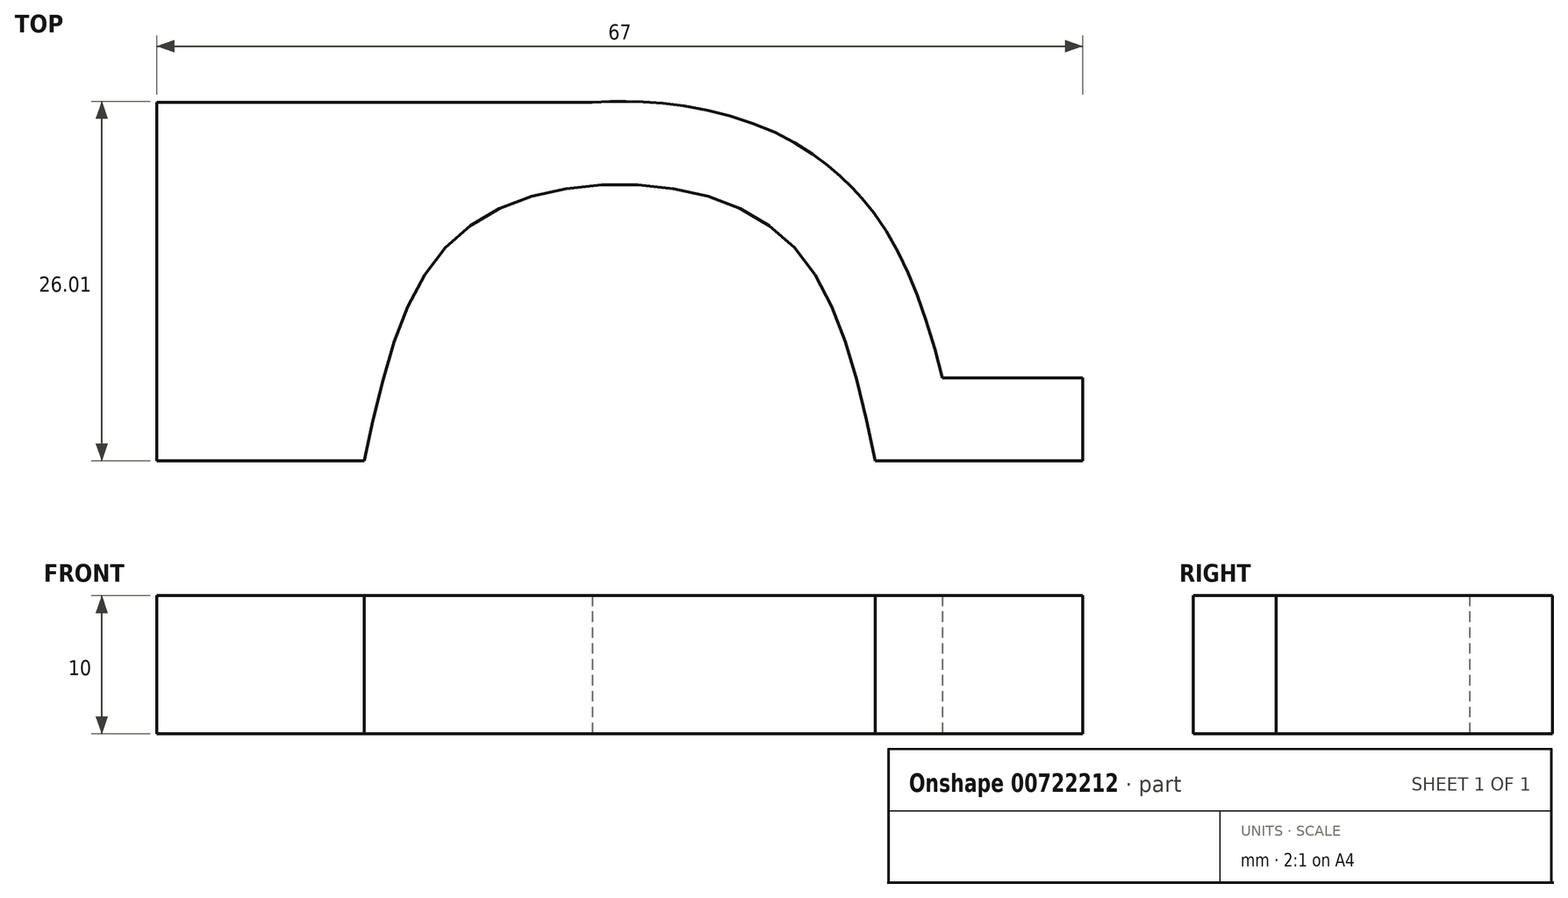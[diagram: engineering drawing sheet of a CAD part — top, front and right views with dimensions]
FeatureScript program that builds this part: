
annotation { "Feature Type Name" : "Feature", "Feature Type Description" : "" }
export const myFeature = defineFeature(function(context is Context, id is Id, definition is map)
    precondition{}
    {
        {
            var Q0;
            Q0=qCreatedBy(makeId("Top.planeOp"),FACE);
            var sketch = newSketch(context, id + "F0", { "sketchPlane" : qUnion([Q0])});
            skFitSpline(sketch, "E0", {"points": [v(-18.5, -20) * mm, v(-12.5, -4.42) * mm, v(0, 0) * mm, v(12.5, -4.42) * mm, v(18.5, -20) * mm], "startDerivative": vector(14.66, 68.17) * mm, "endDerivative": vector(14.66, -68.17) * mm});
            skLineSegment(sketch, "E1", {"start": v(-18.5, -20) * mm, "end": v(-33.5, -20) * mm});
            skLineSegment(sketch, "E2.MirrorCS", {"start": v(18.5, -20) * mm, "end": v(33.5, -20) * mm});
            skLineSegment(sketch, "E3.0", {"start": v(-23.3, -14) * mm, "end": v(-28.5, -14) * mm});
            skFitSpline(sketch, "E3.1", {"points": [v(-24.37, -18.74) * mm, v(-24.06, -17.32) * mm, v(-23.43, -14.39) * mm, v(-22.44, -10.64) * mm, v(-21.38, -7.65) * mm, v(-20.41, -5.43) * mm, v(-19.2, -3.25) * mm, v(-18.08, -1.68) * mm, v(-17.22, -0.68) * mm, v(-16.61, -0.03) * mm, v(-15.81, 0.74) * mm, v(-14.8, 1.57) * mm, v(-13.4, 2.56) * mm, v(-11.57, 3.6) * mm, v(-9.3, 4.55) * mm, v(-6.97, 5.23) * mm, v(-4.64, 5.69) * mm, v(-2.7, 5.9) * mm, v(-1.15, 5.99) * mm, v(0, 6) * mm, v(1.15, 5.99) * mm, v(2.7, 5.9) * mm, v(4.64, 5.69) * mm, v(6.97, 5.23) * mm, v(9.3, 4.55) * mm, v(11.57, 3.6) * mm, v(13.4, 2.56) * mm, v(14.8, 1.57) * mm, v(15.81, 0.74) * mm, v(16.61, -0.03) * mm, v(17.22, -0.68) * mm, v(18.08, -1.68) * mm, v(19.2, -3.25) * mm, v(20.41, -5.43) * mm, v(21.38, -7.65) * mm, v(22.44, -10.64) * mm, v(23.43, -14.39) * mm, v(24.06, -17.32) * mm, v(24.37, -18.74) * mm]});
            skLineSegment(sketch, "E3.2", {"start": v(23.3, -14) * mm, "end": v(28.5, -14) * mm});
            skLineSegment(sketch, "E4", {"start": v(-33.5, -20) * mm, "end": v(-33.5, -14) * mm});
            skLineSegment(sketch, "E5", {"start": v(-33.5, -14) * mm, "end": v(-28.5, -14) * mm});
            skLineSegment(sketch, "E6.MirrorCS", {"start": v(33.5, -20) * mm, "end": v(33.5, -14) * mm});
            skLineSegment(sketch, "E7.MirrorCS", {"start": v(0, -27.5) * mm, "end": v(-5, -27.5) * mm});
            skLineSegment(sketch, "E8", {"start": v(28.5, -14) * mm, "end": v(33.5, -14) * mm});
            skSolve(sketch);
        }
        {
            var Q0;
            Q0 = qSketchRegion(id + "F0", true);
            extrude(context, id + "F1", {"entities" : qUnion([Q0]), "depth" : 10 * mm, "offsetDistance" : 25 * mm});
        }
        {
            var Q0;
            Q0=makeQuery(id+"F1.opExtrude","SWEPT_BODY",BODY,{"disambiguationData":[OSD([sQuery(id+"F0.wireOp",EDGE,"E0"),sQuery(id+"F0.wireOp",EDGE,"E1"),sQuery(id+"F0.wireOp",EDGE,"E2.MirrorCS"),sQuery(id+"F0.wireOp",EDGE,"E3.0"),sQuery(id+"F0.wireOp",EDGE,"E3.1"),sQuery(id+"F0.wireOp",EDGE,"E3.2"),sQuery(id+"F0.wireOp",EDGE,"E4"),sQuery(id+"F0.wireOp",EDGE,"E5"),sQuery(id+"F0.wireOp",EDGE,"E6.MirrorCS"),sQuery(id+"F0.wireOp",EDGE,"E7.MirrorCS")])]});
            var Q1;
            Q1=qCreatedBy(makeId("Right.planeOp"),FACE);
            mirror(context, id + "F2", {"entities" : qUnion([Q0]), "mirrorPlane" : qUnion([Q1])});
        }
        {
            var Q0;
            Q0=makeQuery(id+"F2.opPattern","COPY",FACE,{"derivedFrom":makeQuery(id+"F1.opExtrude","SWEPT_FACE",FACE,{"disambiguationData":[OSD([sQuery(id+"F0.wireOp",EDGE,"E2.MirrorCS")])]}),"instanceName":"1"});
            extrude(context, id + "F3", {"entities" : qUnion([Q0]), "operationType" : NewBodyOperationType.ADD, "oppositeDirection" : true, "depth" : 25.95 * mm, "offsetDistance" : 25 * mm});
        }
        {
            var Q0;
            Q0=makeQuery(id+"F3.opExtrude","SWEPT_FACE",FACE,{"disambiguationData":[OSD([sQuery(id+"F0.wireOp",EDGE,"E0"),sQuery(id+"F0.wireOp",EDGE,"E2.MirrorCS")])]});
            extrude(context, id + "F4", {"entities" : qUnion([Q0]), "operationType" : NewBodyOperationType.ADD, "depth" : 7.7 * mm, "offsetDistance" : 25 * mm});
        }
        {
            var Q0;
            Q0=makeQuery(id+"F4.opExtrude","CAP_FACE",FACE,{"disambiguationData":[OSD([sQuery(id+"F0.wireOp",EDGE,"E0"),sQuery(id+"F0.wireOp",EDGE,"E2.MirrorCS")])],"isStart":false});
            extrude(context, id + "F5", {"entities" : qUnion([Q0]), "operationType" : NewBodyOperationType.ADD, "depth" : 11.7 * mm, "offsetDistance" : 25 * mm});
        }
    });
